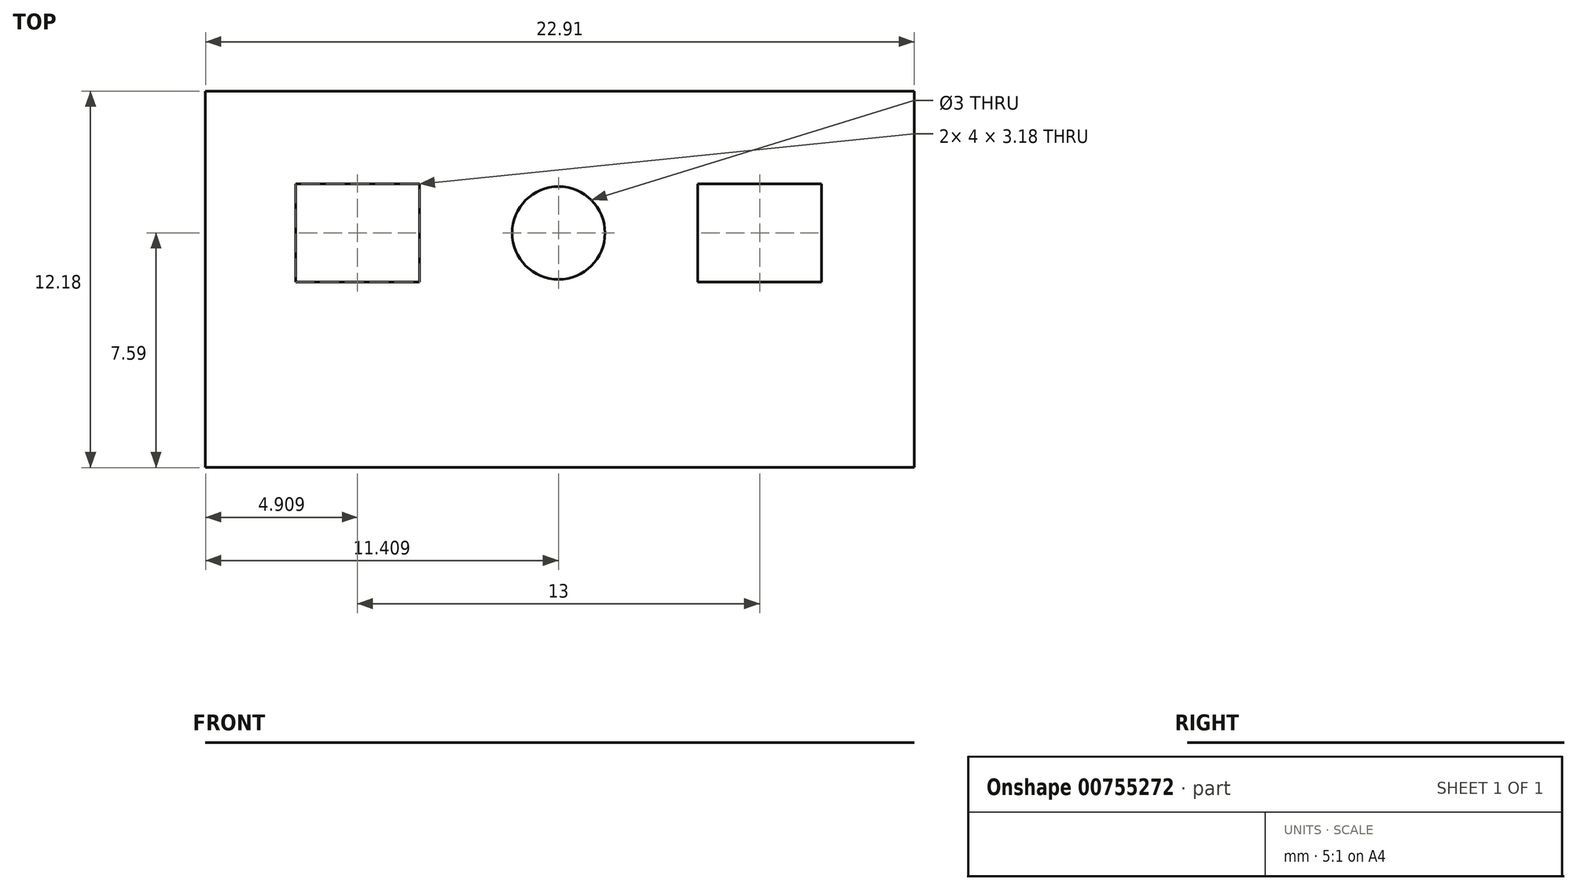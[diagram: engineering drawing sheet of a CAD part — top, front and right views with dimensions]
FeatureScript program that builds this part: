
annotation { "Feature Type Name" : "Feature", "Feature Type Description" : "" }
export const myFeature = defineFeature(function(context is Context, id is Id, definition is map)
    precondition{}
    {
        {
            var Q0;
            Q0=qCreatedBy(makeId("Top.planeOp"),FACE);
            var sketch = newSketch(context, id + "F0", { "sketchPlane" : qUnion([Q0])});
            skCircle(sketch, "E0", {"center": v(-5.78, -26.7) * mm, "radius": 1.5 * mm});
            skLineSegment(sketch, "E1.bottom", {"start": v(-1.28, -25.12) * mm, "end": v(2.72, -25.12) * mm});
            skLineSegment(sketch, "E1.top", {"start": v(-1.28, -28.3) * mm, "end": v(2.72, -28.3) * mm});
            skLineSegment(sketch, "E1.left", {"start": v(-1.28, -25.12) * mm, "end": v(-1.28, -28.3) * mm});
            skLineSegment(sketch, "E1.right", {"start": v(2.72, -25.12) * mm, "end": v(2.72, -28.3) * mm});
            skPoint(sketch, "E1.middle", {"position": v(0.72, -26.7) * mm});
            skLineSegment(sketch, "E2.MirrorCS", {"start": v(-10.28, -25.12) * mm, "end": v(-10.28, -28.3) * mm});
            skLineSegment(sketch, "E3.MirrorCS", {"start": v(-10.28, -25.12) * mm, "end": v(-14.28, -25.12) * mm});
            skLineSegment(sketch, "E4.MirrorCS", {"start": v(-14.28, -25.12) * mm, "end": v(-14.28, -28.3) * mm});
            skLineSegment(sketch, "E5.MirrorCS", {"start": v(-10.28, -28.3) * mm, "end": v(-14.28, -28.3) * mm});
            skLineSegment(sketch, "E6.bottom", {"start": v(-17.2, -34.3) * mm, "end": v(5.72, -34.3) * mm});
            skLineSegment(sketch, "E6.left", {"start": v(-17.2, -34.3) * mm, "end": v(-17.2, -22.12) * mm});
            skLineSegment(sketch, "E6.right", {"start": v(5.72, -34.3) * mm, "end": v(5.72, -22.12) * mm});
            skLineSegment(sketch, "E7.top", {"start": v(-17.2, -22.12) * mm, "end": v(5.72, -22.12) * mm});
            skSolve(sketch);
        }
        {
            var Q0;
            Q0=makeQuery(id+"F0.imprint","IMPRINT",FACE,{"disambiguationData":[TD([[makeQuery(id+"F0.imprint","IMPRINT",EDGE,{"derivedFrom":sQuery(id+"F0.wireOp",EDGE,"E0")}),-1.0]])]});
            extrude(context, id + "F1", {"entities" : qUnion([Q0]), "depth" : 1 / 203.2 * mm, "offsetDistance" : 25 * mm});
        }
    });
